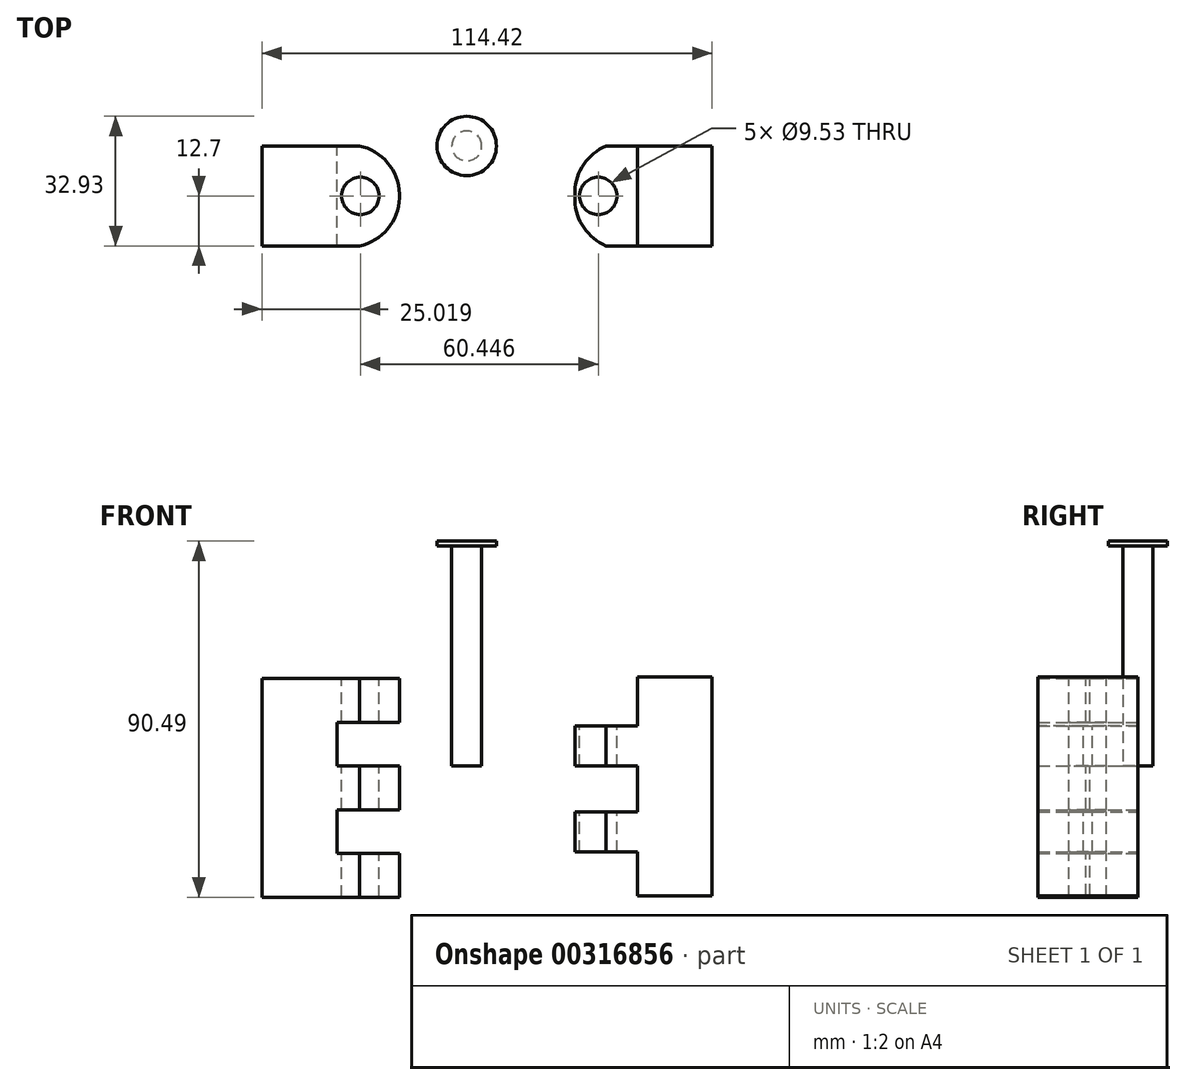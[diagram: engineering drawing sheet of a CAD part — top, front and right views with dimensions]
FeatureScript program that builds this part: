
annotation { "Feature Type Name" : "Feature", "Feature Type Description" : "" }
export const myFeature = defineFeature(function(context is Context, id is Id, definition is map)
    precondition{}
    {
        {
            var Q0;
            Q0=qCreatedBy(makeId("Front.planeOp"),FACE);
            var sketch = newSketch(context, id + "F0", { "sketchPlane" : qUnion([Q0])});
            skLineSegment(sketch, "E0.bottom", {"start": v(-52.05, 22.23) * mm, "end": v(-33, 22.23) * mm});
            skLineSegment(sketch, "E0.top", {"start": v(-52.05, -33.34) * mm, "end": v(-33, -33.34) * mm});
            skLineSegment(sketch, "E0.left", {"start": v(-52.05, 22.23) * mm, "end": v(-52.05, -33.34) * mm});
            skLineSegment(sketch, "E0.right", {"start": v(-33, 22.23) * mm, "end": v(-33, -33.34) * mm});
            skLineSegment(sketch, "E1.bottom", {"start": v(-33, 22.23) * mm, "end": v(-17.13, 22.23) * mm});
            skLineSegment(sketch, "E1.top", {"start": v(-33, 11.11) * mm, "end": v(-17.13, 11.11) * mm});
            skLineSegment(sketch, "E1.left", {"start": v(-33, 22.23) * mm, "end": v(-33, 11.11) * mm});
            skLineSegment(sketch, "E1.right", {"start": v(-17.13, 22.23) * mm, "end": v(-17.13, 11.11) * mm});
            skLineSegment(sketch, "E2.bottom", {"start": v(-33, 0) * mm, "end": v(-17.13, 0) * mm});
            skLineSegment(sketch, "E2.top", {"start": v(-33, -11.11) * mm, "end": v(-17.13, -11.11) * mm});
            skLineSegment(sketch, "E2.left", {"start": v(-33, 0) * mm, "end": v(-33, -11.11) * mm});
            skLineSegment(sketch, "E2.right", {"start": v(-17.13, 0) * mm, "end": v(-17.13, -11.11) * mm});
            skLineSegment(sketch, "E3.bottom", {"start": v(-33, -33.34) * mm, "end": v(-17.13, -33.34) * mm});
            skLineSegment(sketch, "E3.top", {"start": v(-33, -22.23) * mm, "end": v(-17.13, -22.23) * mm});
            skLineSegment(sketch, "E3.left", {"start": v(-33, -33.34) * mm, "end": v(-33, -22.23) * mm});
            skLineSegment(sketch, "E3.right", {"start": v(-17.13, -33.34) * mm, "end": v(-17.13, -22.23) * mm});
            skSolve(sketch);
        }
        {
            var Q0;
            Q0=makeQuery(id+"F0.imprint","IMPRINT",FACE,{"disambiguationData":[TD([[makeQuery(id+"F0.imprint","IMPRINT",EDGE,{"derivedFrom":sQuery(id+"F0.wireOp",EDGE,"E0.bottom")}),-1.0]])]});
            var Q1;
            Q1=makeQuery(id+"F0.imprint","IMPRINT",FACE,{"disambiguationData":[TD([[makeQuery(id+"F0.imprint","IMPRINT",EDGE,{"derivedFrom":sQuery(id+"F0.wireOp",EDGE,"E1.bottom")}),-1.0]])]});
            var Q2;
            Q2=makeQuery(id+"F0.imprint","IMPRINT",FACE,{"disambiguationData":[TD([[makeQuery(id+"F0.imprint","IMPRINT",EDGE,{"derivedFrom":sQuery(id+"F0.wireOp",EDGE,"E2.bottom")}),-1.0]])]});
            var Q3;
            Q3=makeQuery(id+"F0.imprint","IMPRINT",FACE,{"disambiguationData":[TD([[makeQuery(id+"F0.imprint","IMPRINT",EDGE,{"derivedFrom":sQuery(id+"F0.wireOp",EDGE,"E3.bottom")}),1.0]])]});
            extrude(context, id + "F1", {"entities" : qUnion([Q0, Q1, Q2, Q3]), "depth" : 25.4 * mm});
        }
        {
            var Q0;
            Q0=makeQuery(id+"F1.opExtrude","SWEPT_FACE",FACE,{"disambiguationData":[OSD([sQuery(id+"F0.wireOp",EDGE,"E0.bottom"),sQuery(id+"F0.wireOp",EDGE,"E1.bottom")])]});
            var sketch = newSketch(context, id + "F2", { "sketchPlane" : qUnion([Q0])});
            skPoint(sketch, "E4", {"position": v(-27.03, -12.7) * mm});
            skSolve(sketch);
        }
        {
            var Q0;
            Q0=sQuery(id+"F2.wireOp",VERTEX,"E4");
            var Q1;
            Q1=makeQuery(id+"F1.opExtrude","SWEPT_BODY",BODY,{"disambiguationData":[OSD([sQuery(id+"F0.wireOp",EDGE,"E0.bottom"),sQuery(id+"F0.wireOp",EDGE,"E0.top"),sQuery(id+"F0.wireOp",EDGE,"E0.left"),sQuery(id+"F0.wireOp",EDGE,"E0.right"),sQuery(id+"F0.wireOp",EDGE,"E1.bottom"),sQuery(id+"F0.wireOp",EDGE,"E1.top"),sQuery(id+"F0.wireOp",EDGE,"E1.right"),sQuery(id+"F0.wireOp",EDGE,"E2.bottom"),sQuery(id+"F0.wireOp",EDGE,"E2.top"),sQuery(id+"F0.wireOp",EDGE,"E2.right"),sQuery(id+"F0.wireOp",EDGE,"E3.bottom"),sQuery(id+"F0.wireOp",EDGE,"E3.top"),sQuery(id+"F0.wireOp",EDGE,"E3.right")])]});
            hole(context, id + "F3", {"style" : HoleStyle.SIMPLE, "endStyle" : HoleEndStyle.THROUGH, "holeDiameter" : 9.52 * mm, "tappedDepth" : 12.7 * mm, "tapClearance" : 3, "locations" : qUnion([Q0]), "scope" : qUnion([Q1])});
        }
        {
            var Q0;
            Q0=qCreatedBy(makeId("Front.planeOp"),FACE);
            var sketch = newSketch(context, id + "F4", { "sketchPlane" : qUnion([Q0])});
            skLineSegment(sketch, "E5.bottom", {"start": v(62.37, 22.6) * mm, "end": v(43.32, 22.6) * mm});
            skLineSegment(sketch, "E5.top", {"start": v(62.37, -32.96) * mm, "end": v(43.32, -32.96) * mm});
            skLineSegment(sketch, "E5.left", {"start": v(62.37, 22.6) * mm, "end": v(62.37, -32.96) * mm});
            skLineSegment(sketch, "E5.right", {"start": v(43.32, 22.6) * mm, "end": v(43.32, -32.96) * mm});
            skLineSegment(sketch, "E6.bottom", {"start": v(43.32, 10.16) * mm, "end": v(27.45, 10.16) * mm});
            skLineSegment(sketch, "E6.top", {"start": v(43.32, 0) * mm, "end": v(27.45, 0) * mm});
            skLineSegment(sketch, "E6.left", {"start": v(43.32, 10.16) * mm, "end": v(43.32, 0) * mm});
            skLineSegment(sketch, "E6.right", {"start": v(27.45, 10.16) * mm, "end": v(27.45, 0) * mm});
            skLineSegment(sketch, "E7.bottom", {"start": v(43.32, -11.68) * mm, "end": v(27.45, -11.68) * mm});
            skLineSegment(sketch, "E7.top", {"start": v(43.32, -21.84) * mm, "end": v(27.45, -21.84) * mm});
            skLineSegment(sketch, "E7.left", {"start": v(43.32, -11.68) * mm, "end": v(43.32, -21.84) * mm});
            skLineSegment(sketch, "E7.right", {"start": v(27.45, -11.68) * mm, "end": v(27.45, -21.84) * mm});
            skSolve(sketch);
        }
        {
            var Q0;
            {var subQ1=sQuery(id+"F4.wireOp",EDGE,"E5.bottom");Q0=makeQuery(id+"F4.imprint","IMPRINT",FACE,{"disambiguationData":[TD([[makeQuery(id+"F4.imprint","IMPRINT",EDGE,{"derivedFrom":subQ1}),1.0]])]});}
            var Q1;
            Q1=makeQuery(id+"F4.imprint","IMPRINT",FACE,{"disambiguationData":[TD([[makeQuery(id+"F4.imprint","IMPRINT",EDGE,{"derivedFrom":sQuery(id+"F4.wireOp",EDGE,"E6.bottom")}),1.0]])]});
            var Q2;
            Q2=makeQuery(id+"F4.imprint","IMPRINT",FACE,{"disambiguationData":[TD([[makeQuery(id+"F4.imprint","IMPRINT",EDGE,{"derivedFrom":sQuery(id+"F4.wireOp",EDGE,"E7.bottom")}),1.0]])]});
            extrude(context, id + "F5", {"entities" : qUnion([Q0, Q1, Q2]), "depth" : 25.4 * mm});
        }
        {
            var Q0;
            Q0=makeQuery(id+"F5.opExtrude","SWEPT_FACE",FACE,{"disambiguationData":[OSD([sQuery(id+"F4.wireOp",EDGE,"E6.bottom")])]});
            var sketch = newSketch(context, id + "F6", { "sketchPlane" : qUnion([Q0])});
            skPoint(sketch, "E8", {"position": v(33.41, -12.7) * mm});
            skSolve(sketch);
        }
        {
            var Q0;
            Q0=sQuery(id+"F6.wireOp",VERTEX,"E8");
            var Q1;
            Q1=makeQuery(id+"F5.opExtrude","SWEPT_BODY",BODY,{"disambiguationData":[OSD([sQuery(id+"F4.wireOp",EDGE,"E5.bottom"),sQuery(id+"F4.wireOp",EDGE,"E5.top"),sQuery(id+"F4.wireOp",EDGE,"E5.left"),sQuery(id+"F4.wireOp",EDGE,"E5.right"),sQuery(id+"F4.wireOp",EDGE,"E6.bottom"),sQuery(id+"F4.wireOp",EDGE,"E6.top"),sQuery(id+"F4.wireOp",EDGE,"E6.right"),sQuery(id+"F4.wireOp",EDGE,"E7.bottom"),sQuery(id+"F4.wireOp",EDGE,"E7.top"),sQuery(id+"F4.wireOp",EDGE,"E7.right")])]});
            hole(context, id + "F7", {"style" : HoleStyle.SIMPLE, "endStyle" : HoleEndStyle.THROUGH, "holeDiameter" : 9.52 * mm, "tappedDepth" : 12.7 * mm, "tapClearance" : 3, "locations" : qUnion([Q0]), "scope" : qUnion([Q1])});
        }
        {
            var Q0;
            Q0=qCreatedBy(makeId("Top.planeOp"),FACE);
            var sketch = newSketch(context, id + "F8", { "sketchPlane" : qUnion([Q0])});
            skCircle(sketch, "E9", {"center": v(0, 0) * mm, "radius": 3.81 * mm});
            skSolve(sketch);
        }
        {
            var Q0;
            Q0 = qSketchRegion(id + "F8", true);
            extrude(context, id + "F9", {"entities" : qUnion([Q0]), "depth" : 55.88 * mm});
        }
        {
            var Q0;
            Q0=makeQuery(id+"F9.opExtrude","CAP_FACE",FACE,{"disambiguationData":[OSD([sQuery(id+"F8.wireOp",EDGE,"E9")])],"isStart":false});
            var sketch = newSketch(context, id + "F10", { "sketchPlane" : qUnion([Q0])});
            skCircle(sketch, "E10", {"center": v(0, 0) * mm, "radius": 7.53 * mm});
            skSolve(sketch);
        }
        {
            var Q0;
            Q0=makeQuery(id+"F10.imprint","IMPRINT",FACE,{"disambiguationData":[TD([[makeQuery(id+"F10.imprint","IMPRINT",EDGE,{"derivedFrom":sQuery(id+"F10.wireOp",EDGE,"E10")}),1.0]])]});
            var Q1;
            Q1=makeQuery(id+"F10.imprint","IMPRINT",FACE,{"disambiguationData":[TD([[makeQuery(id+"F10.imprint","IMPRINT",EDGE,{"derivedFrom":makeQuery(id+"F9.opExtrude","CAP_EDGE",EDGE,{"disambiguationData":[OSD([sQuery(id+"F8.wireOp",EDGE,"E9")])],"isStart":false})}),1.0]])]});
            extrude(context, id + "F11", {"entities" : qUnion([Q0, Q1]), "operationType" : NewBodyOperationType.ADD, "depth" : 1.27 * mm});
        }
        {
            var Q0;
            Q0=makeQuery(id+"F1.opExtrude","SWEPT_FACE",FACE,{"disambiguationData":[OSD([sQuery(id+"F0.wireOp",EDGE,"E0.bottom"),sQuery(id+"F0.wireOp",EDGE,"E1.bottom")])]});
            var sketch = newSketch(context, id + "F12", { "sketchPlane" : qUnion([Q0])});
            skArc(sketch, "E11", {"start": v(-17.13, -12.7) * mm, "mid": v(-19.9, -4.51) * mm, "end": v(-27.29, 0) * mm});
            skArc(sketch, "E12", {"start": v(-27.29, -25.4) * mm, "mid": v(-19.9, -20.89) * mm, "end": v(-17.13, -12.7) * mm});
            skLineSegment(sketch, "E13", {"start": v(-27.29, 0) * mm, "end": v(-11.2, 0) * mm});
            skLineSegment(sketch, "E14", {"start": v(-11.2, 0) * mm, "end": v(-11.2, -25.56) * mm});
            skLineSegment(sketch, "E15", {"start": v(-11.2, -25.56) * mm, "end": v(-27.29, -25.4) * mm});
            skSolve(sketch);
        }
        {
            var Q0;
            {var subQ1=sQuery(id+"F12.wireOp",EDGE,"E11");var subQ2=sQuery(id+"F0.wireOp",EDGE,"E1.bottom");var subQ4=makeQuery(id+"F1.opExtrude","SWEPT_EDGE",EDGE,{"disambiguationData":[OSD([subQ2,sQuery(id+"F0.wireOp",EDGE,"E1.right")])]});var subQ5=makeQuery(id+"F12.imprint","INTERSECT",VERTEX,{"derivedFrom":[subQ4,subQ1]});Q0=makeQuery(id+"F12.imprint","IMPRINT",FACE,{"disambiguationData":[TD([[makeQuery(id+"F12.imprint","IMPRINT",EDGE,{"disambiguationData":[TD([[subQ5,-1.0]])],"derivedFrom":subQ1}),-1.0]])]});}
            var Q1;
            {var subQ0=sQuery(id+"F12.wireOp",EDGE,"E12");var subQ1=sQuery(id+"F0.wireOp",EDGE,"E1.bottom");var subQ4=makeQuery(id+"F1.opExtrude","SWEPT_EDGE",EDGE,{"disambiguationData":[OSD([subQ1,sQuery(id+"F0.wireOp",EDGE,"E1.right")])]});var subQ5=makeQuery(id+"F12.imprint","INTERSECT",VERTEX,{"derivedFrom":[subQ4,subQ0]});Q1=makeQuery(id+"F12.imprint","IMPRINT",FACE,{"disambiguationData":[TD([[makeQuery(id+"F12.imprint","IMPRINT",EDGE,{"disambiguationData":[TD([[subQ5,1.0]])],"derivedFrom":subQ0}),-1.0]])]});}
            extrude(context, id + "F13", {"entities" : qUnion([Q0, Q1]), "operationType" : NewBodyOperationType.REMOVE, "oppositeDirection" : true, "depth" : 76.2 * mm});
        }
        {
            var Q0;
            Q0=makeQuery(id+"F5.opExtrude","SWEPT_FACE",FACE,{"disambiguationData":[OSD([sQuery(id+"F4.wireOp",EDGE,"E6.bottom")])]});
            var sketch = newSketch(context, id + "F14", { "sketchPlane" : qUnion([Q0])});
            skArc(sketch, "E16", {"start": v(27.45, -12.7) * mm, "mid": v(29.44, -20.29) * mm, "end": v(35.38, -25.4) * mm});
            skArc(sketch, "E17", {"start": v(35.38, 0) * mm, "mid": v(29.45, -5.12) * mm, "end": v(27.45, -12.7) * mm});
            skLineSegment(sketch, "E18", {"start": v(35.38, 0) * mm, "end": v(27.45, 0) * mm});
            skLineSegment(sketch, "E19", {"start": v(35.38, 0) * mm, "end": v(21.63, 0) * mm});
            skLineSegment(sketch, "E20", {"start": v(21.63, 0) * mm, "end": v(21.63, -25.4) * mm});
            skLineSegment(sketch, "E21", {"start": v(21.63, -25.4) * mm, "end": v(35.38, -25.4) * mm});
            skSolve(sketch);
        }
        {
            var Q0;
            {var subQ0=sQuery(id+"F14.wireOp",EDGE,"E19");var subQ1=sQuery(id+"F14.wireOp",EDGE,"E17");var subQ2=sQuery(id+"F4.wireOp",EDGE,"E6.bottom");var subQ3=makeQuery(id+"F14.imprint","INTERSECT",VERTEX,{"derivedFrom":[makeQuery(id+"F5.opExtrude","CAP_EDGE",EDGE,{"disambiguationData":[OSD([subQ2])],"isStart":true}),subQ1,subQ0]});Q0=makeQuery(id+"F14.imprint","IMPRINT",FACE,{"disambiguationData":[TD([[makeQuery(id+"F14.imprint","IMPRINT",EDGE,{"disambiguationData":[TD([[subQ3,-1.0]])],"derivedFrom":subQ1}),-1.0]])]});}
            var Q1;
            {var subQ0=sQuery(id+"F14.wireOp",EDGE,"E21");var subQ1=sQuery(id+"F14.wireOp",EDGE,"E16");var subQ2=sQuery(id+"F4.wireOp",EDGE,"E6.bottom");var subQ3=makeQuery(id+"F14.imprint","INTERSECT",VERTEX,{"derivedFrom":[makeQuery(id+"F5.opExtrude","CAP_EDGE",EDGE,{"disambiguationData":[OSD([subQ2])],"isStart":false}),subQ1,subQ0]});Q1=makeQuery(id+"F14.imprint","IMPRINT",FACE,{"disambiguationData":[TD([[makeQuery(id+"F14.imprint","IMPRINT",EDGE,{"disambiguationData":[TD([[subQ3,1.0]])],"derivedFrom":subQ1}),-1.0]])]});}
            extrude(context, id + "F15", {"entities" : qUnion([Q0, Q1]), "operationType" : NewBodyOperationType.REMOVE, "oppositeDirection" : true, "depth" : 76.2 * mm});
        }
    });
